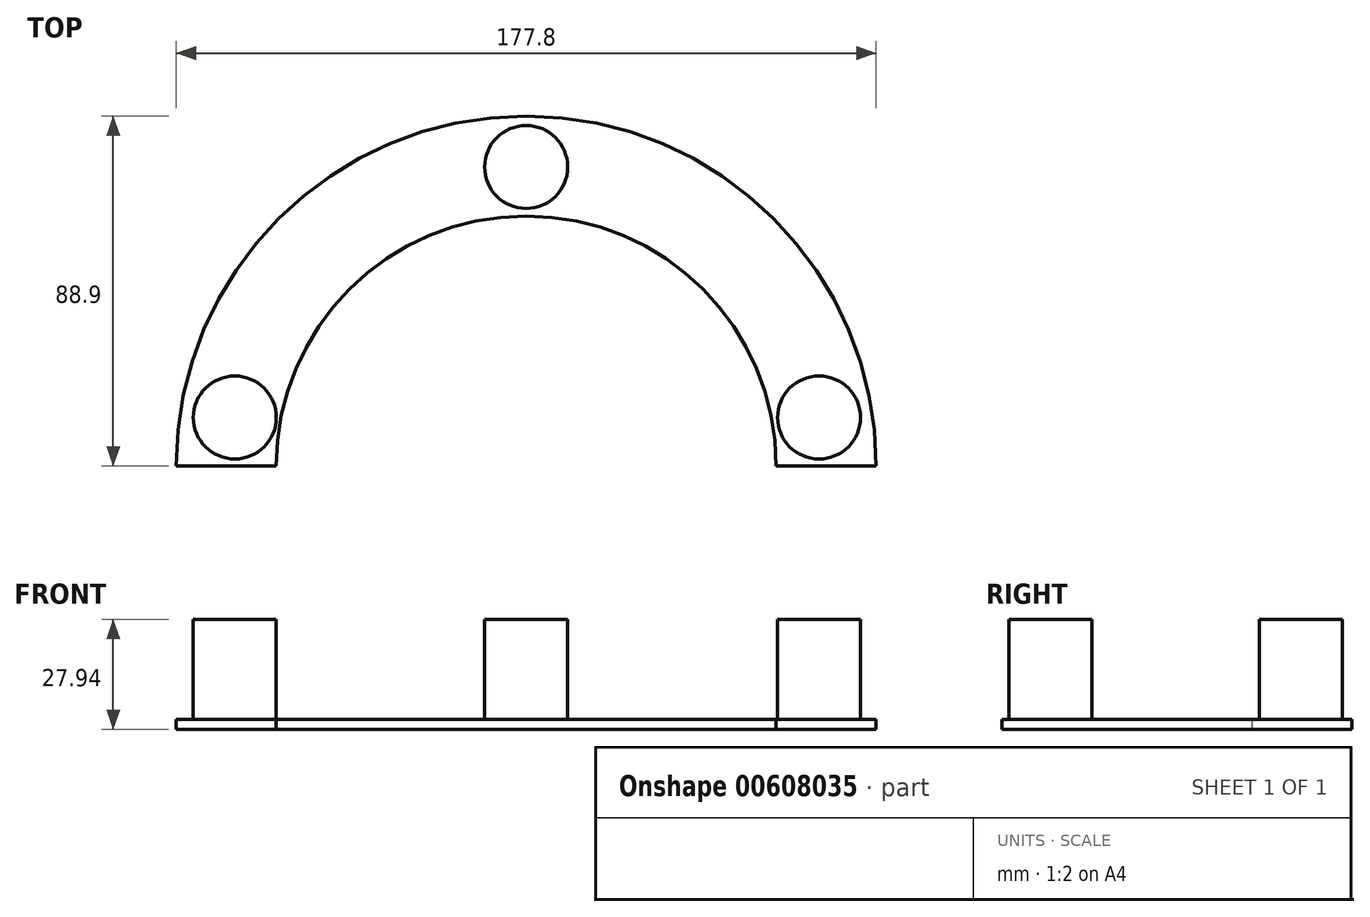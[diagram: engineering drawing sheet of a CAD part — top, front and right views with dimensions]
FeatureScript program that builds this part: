
annotation { "Feature Type Name" : "Feature", "Feature Type Description" : "" }
export const myFeature = defineFeature(function(context is Context, id is Id, definition is map)
    precondition{}
    {
        {
            var Q0;
            Q0=qCreatedBy(makeId("Top.planeOp"),FACE);
            var sketch = newSketch(context, id + "F0", { "sketchPlane" : qUnion([Q0])});
            skArc(sketch, "E0", {"start": v(88.9, 0) * mm, "mid": v(0, 88.9) * mm, "end": v(-88.9, 0) * mm});
            skArc(sketch, "E1", {"start": v(63.5, 0) * mm, "mid": v(0, 63.5) * mm, "end": v(-63.5, 0) * mm});
            skLineSegment(sketch, "E2", {"start": v(-63.5, 0) * mm, "end": v(-88.9, 0) * mm});
            skLineSegment(sketch, "E3", {"start": v(88.9, 0) * mm, "end": v(63.5, 0) * mm});
            skSolve(sketch);
        }
        {
            var Q0;
            Q0=makeQuery(id+"F0.imprint","IMPRINT",FACE,{"disambiguationData":[TD([[makeQuery(id+"F0.imprint","IMPRINT",EDGE,{"derivedFrom":sQuery(id+"F0.wireOp",EDGE,"E0")}),1.0]])]});
            extrude(context, id + "F1", {"entities" : qUnion([Q0]), "depth" : 2.54 * mm, "offsetDistance" : 25.4 * mm});
        }
        {
            var Q0;
            Q0=makeQuery(id+"F1.opExtrude","CAP_FACE",FACE,{"disambiguationData":[OSD([sQuery(id+"F0.wireOp",EDGE,"E0"),sQuery(id+"F0.wireOp",EDGE,"E1"),sQuery(id+"F0.wireOp",EDGE,"E2"),sQuery(id+"F0.wireOp",EDGE,"E3")])],"isStart":false});
            var sketch = newSketch(context, id + "F2", { "sketchPlane" : qUnion([Q0])});
            skLineSegment(sketch, "E4", {"start": v(-85.2, 25.4) * mm, "end": v(85.2, 25.4) * mm, "construction": true});
            skLineSegment(sketch, "E5", {"start": v(-85.2, 25.4) * mm, "end": v(-63.5, 0) * mm, "construction": true});
            skLineSegment(sketch, "E6", {"start": v(-88.9, 0) * mm, "end": v(-58.2, 25.4) * mm, "construction": true});
            skCircle(sketch, "E7", {"center": v(-74.02, 12.31) * mm, "radius": 10.54 * mm});
            skCircle(sketch, "E8", {"center": v(74.4, 12.31) * mm, "radius": 10.54 * mm});
            skCircle(sketch, "E9", {"center": v(0, 75.96) * mm, "radius": 10.54 * mm});
            skSolve(sketch);
        }
        {
            var Q0;
            Q0=makeQuery(id+"F2.imprint","IMPRINT",FACE,{"disambiguationData":[TD([[makeQuery(id+"F2.imprint","IMPRINT",EDGE,{"derivedFrom":sQuery(id+"F2.wireOp",EDGE,"E9")}),1.0]])]});
            var Q1;
            Q1=makeQuery(id+"F2.imprint","IMPRINT",FACE,{"disambiguationData":[TD([[makeQuery(id+"F2.imprint","IMPRINT",EDGE,{"derivedFrom":sQuery(id+"F2.wireOp",EDGE,"E7")}),1.0]])]});
            var Q2;
            Q2=makeQuery(id+"F2.imprint","IMPRINT",FACE,{"disambiguationData":[TD([[makeQuery(id+"F2.imprint","IMPRINT",EDGE,{"derivedFrom":sQuery(id+"F2.wireOp",EDGE,"E8")}),1.0]])]});
            extrude(context, id + "F3", {"entities" : qUnion([Q0, Q1, Q2]), "operationType" : NewBodyOperationType.ADD, "depth" : 25.4 * mm, "offsetDistance" : 25.4 * mm});
        }
    });
